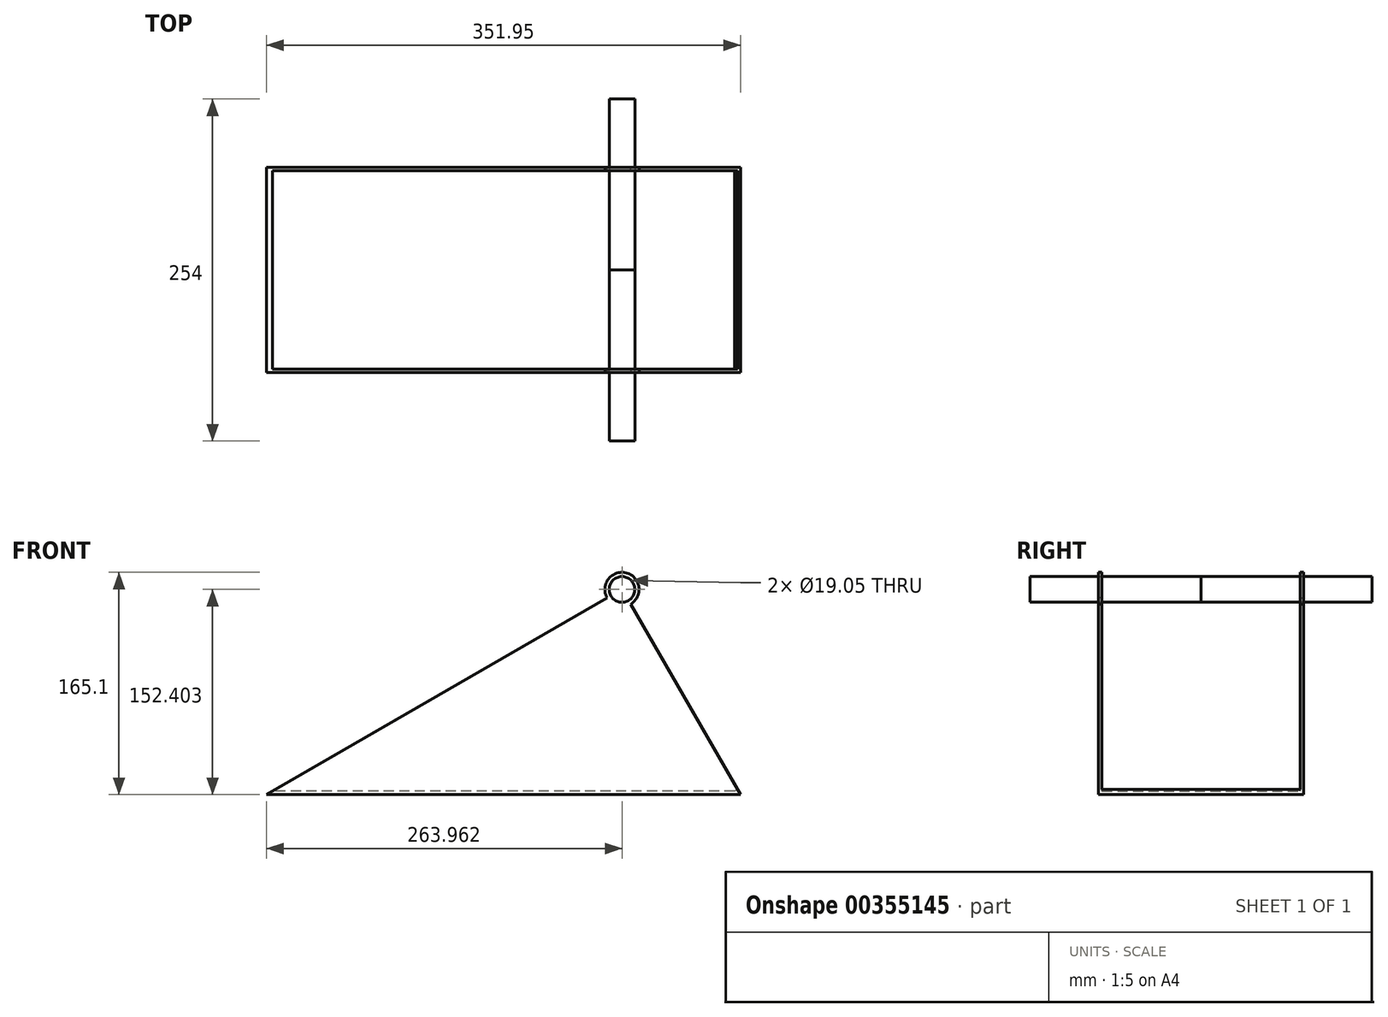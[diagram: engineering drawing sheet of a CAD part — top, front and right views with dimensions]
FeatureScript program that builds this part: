
annotation { "Feature Type Name" : "Feature", "Feature Type Description" : "" }
export const myFeature = defineFeature(function(context is Context, id is Id, definition is map)
    precondition{}
    {
        {
            var Q0;
            Q0=qCreatedBy(makeId("Front.planeOp"),FACE);
            var sketch = newSketch(context, id + "F0", { "sketchPlane" : qUnion([Q0])});
            skLineSegment(sketch, "E0", {"start": v(-6.3, -162.3) * mm, "end": v(-358.26, -162.3) * mm});
            skLineSegment(sketch, "E1", {"start": v(-358.26, -162.3) * mm, "end": v(-94.3, -9.9) * mm});
            skLineSegment(sketch, "E2", {"start": v(-94.3, -9.9) * mm, "end": v(-6.3, -162.3) * mm});
            skLineSegment(sketch, "E3", {"start": v(-94.3, -9.9) * mm, "end": v(58.1, 78.08) * mm, "construction": true});
            skLineSegment(sketch, "E4", {"start": v(58.1, 78.08) * mm, "end": v(-6.3, -162.3) * mm, "construction": true});
            skSolve(sketch);
        }
        {
            var Q0;
            Q0 = qSketchRegion(id + "F0", true);
            extrude(context, id + "F1", {"entities" : qUnion([Q0]), "endBound" : BoundingType.SYMMETRIC, "depth" : 152.4 * mm});
        }
        {
            var Q0;
            Q0=makeQuery(id+"F1.opExtrude","SWEPT_FACE",FACE,{"disambiguationData":[OSD([sQuery(id+"F0.wireOp",EDGE,"E1")])]});
            shell(context, id + "F2", {"entities" : qUnion([Q0]), "thickness" : 2.54 * mm});
        }
        {
            var Q0;
            Q0=makeQuery(id+"F2.opShell","OFFSET_FACE",FACE,{"disambiguationData":[OSD([sQuery(id+"F0.wireOp",EDGE,"E2")])]});
            extrude(context, id + "F3", {"entities" : qUnion([Q0]), "operationType" : NewBodyOperationType.REMOVE, "oppositeDirection" : true, "depth" : 2.54 * mm});
        }
        {
            var Q0;
            Q0=makeQuery(id+"F1.opExtrude","CAP_FACE",FACE,{"disambiguationData":[OSD([sQuery(id+"F0.wireOp",EDGE,"E0"),sQuery(id+"F0.wireOp",EDGE,"E1"),sQuery(id+"F0.wireOp",EDGE,"E2")])],"isStart":false});
            var sketch = newSketch(context, id + "F4", { "sketchPlane" : qUnion([Q0])});
            skCircle(sketch, "E5", {"center": v(-94.3, -9.9) * mm, "radius": 12.7 * mm});
            skCircle(sketch, "E6", {"center": v(-94.3, -9.9) * mm, "radius": 9.53 * mm});
            skLineSegment(sketch, "E7", {"start": v(-102.55, -14.67) * mm, "end": v(-105.3, -16.26) * mm});
            skLineSegment(sketch, "E8", {"start": v(-89.54, -18.16) * mm, "end": v(-87.95, -20.9) * mm});
            skLineSegment(sketch, "E9", {"start": v(-102.55, -14.67) * mm, "end": v(-94.3, -9.9) * mm});
            skLineSegment(sketch, "E10", {"start": v(-89.54, -18.16) * mm, "end": v(-94.3, -9.9) * mm});
            skLineSegment(sketch, "E11", {"start": v(-105.3, -16.26) * mm, "end": v(-124.54, -27.37) * mm});
            skCircle(sketch, "E12", {"center": v(-124.54, -27.37) * mm, "radius": 9.53 * mm});
            skLineSegment(sketch, "E13", {"start": v(-105.3, -16.26) * mm, "end": v(-116.3, -22.6) * mm});
            skSolve(sketch);
        }
        {
            var Q0;
            {var subQ0=sQuery(id+"F4.wireOp",EDGE,"E7");Q0=makeQuery(id+"F4.imprint","IMPRINT",FACE,{"disambiguationData":[TD([[makeQuery(id+"F4.imprint","IMPRINT",EDGE,{"derivedFrom":subQ0}),1.0]])]});}
            extrude(context, id + "F5", {"entities" : qUnion([Q0]), "operationType" : NewBodyOperationType.ADD, "oppositeDirection" : true, "depth" : 2.54 * mm});
        }
        {
            var Q0;
            {var subQ0=sQuery(id+"F4.wireOp",EDGE,"E9");Q0=makeQuery(id+"F4.imprint","IMPRINT",FACE,{"disambiguationData":[TD([[makeQuery(id+"F4.imprint","IMPRINT",EDGE,{"derivedFrom":subQ0}),-1.0]])]});}
            extrude(context, id + "F6", {"entities" : qUnion([Q0]), "operationType" : NewBodyOperationType.REMOVE, "oppositeDirection" : true, "depth" : 2.54 * mm});
        }
        {
            var Q0;
            Q0=makeQuery(id+"F1.opExtrude","CAP_FACE",FACE,{"disambiguationData":[OSD([sQuery(id+"F0.wireOp",EDGE,"E0"),sQuery(id+"F0.wireOp",EDGE,"E1"),sQuery(id+"F0.wireOp",EDGE,"E2")])],"isStart":true});
            var sketch = newSketch(context, id + "F7", { "sketchPlane" : qUnion([Q0])});
            skCircle(sketch, "E14", {"center": v(94.3, -9.9) * mm, "radius": 12.7 * mm});
            skCircle(sketch, "E15", {"center": v(94.3, -9.9) * mm, "radius": 9.53 * mm});
            skLineSegment(sketch, "E16", {"start": v(87.95, -20.9) * mm, "end": v(89.54, -18.16) * mm});
            skLineSegment(sketch, "E17", {"start": v(94.3, -9.9) * mm, "end": v(102.55, -14.67) * mm});
            skLineSegment(sketch, "E18", {"start": v(102.55, -14.67) * mm, "end": v(105.3, -16.26) * mm});
            skLineSegment(sketch, "E19", {"start": v(89.54, -18.16) * mm, "end": v(94.3, -9.9) * mm});
            skLineSegment(sketch, "E20", {"start": v(87.95, -20.9) * mm, "end": v(50.3, -86.1) * mm});
            skSolve(sketch);
        }
        {
            var Q0;
            {var subQ0=sQuery(id+"F7.wireOp",EDGE,"E16");Q0=makeQuery(id+"F7.imprint","IMPRINT",FACE,{"disambiguationData":[TD([[makeQuery(id+"F7.imprint","IMPRINT",EDGE,{"derivedFrom":subQ0}),-1.0]])]});}
            extrude(context, id + "F8", {"entities" : qUnion([Q0]), "operationType" : NewBodyOperationType.ADD, "oppositeDirection" : true, "depth" : 2.54 * mm});
        }
        {
            var Q0;
            {var subQ2=sQuery(id+"F7.wireOp",EDGE,"E17");Q0=makeQuery(id+"F7.imprint","IMPRINT",FACE,{"disambiguationData":[TD([[makeQuery(id+"F7.imprint","IMPRINT",EDGE,{"derivedFrom":subQ2}),1.0]])]});}
            extrude(context, id + "F9", {"entities" : qUnion([Q0]), "operationType" : NewBodyOperationType.REMOVE, "oppositeDirection" : true, "depth" : 2.54 * mm});
        }
        {
            var Q0;
            Q0=qCreatedBy(makeId("Front.planeOp"),FACE);
            var sketch = newSketch(context, id + "F10", { "sketchPlane" : qUnion([Q0])});
            skCircle(sketch, "E21", {"center": v(-94.3, -9.9) * mm, "radius": 9.53 * mm});
            skSolve(sketch);
        }
        {
            var Q0;
            Q0 = qSketchRegion(id + "F10", true);
            extrude(context, id + "F11", {"entities" : qUnion([Q0]), "depth" : 127 * mm});
        }
        {
            var Q0;
            Q0=makeQuery(id+"F11.opExtrude","CAP_FACE",FACE,{"disambiguationData":[OSD([sQuery(id+"F10.wireOp",EDGE,"E21")])],"isStart":true});
            extrude(context, id + "F12", {"entities" : qUnion([Q0]), "depth" : 127 * mm});
        }
    });
